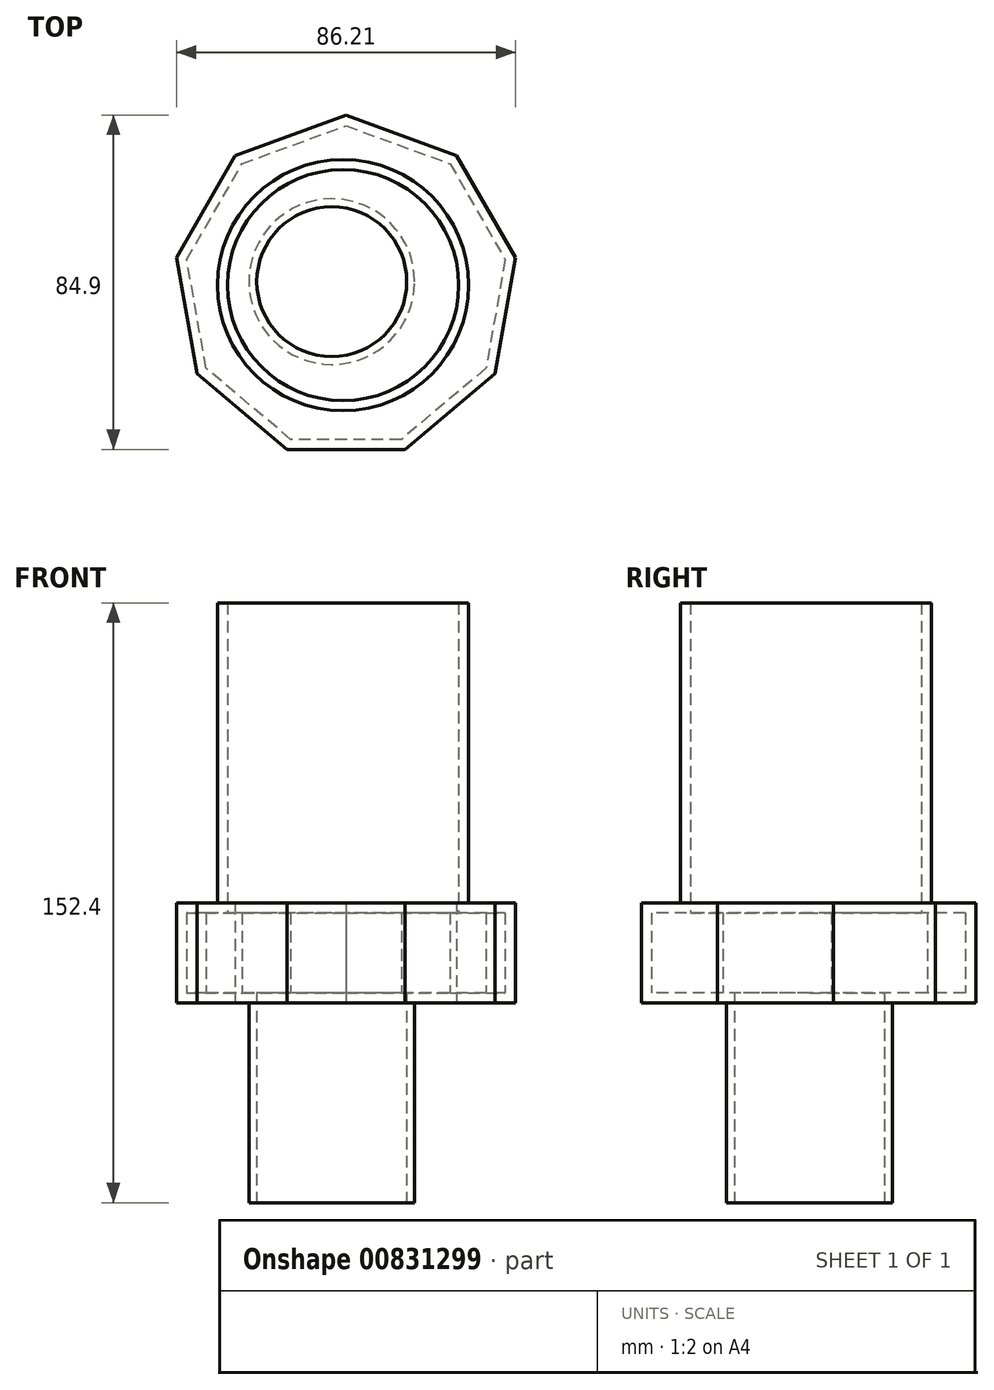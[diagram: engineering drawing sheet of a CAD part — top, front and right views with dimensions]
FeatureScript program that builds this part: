
annotation { "Feature Type Name" : "Feature", "Feature Type Description" : "" }
export const myFeature = defineFeature(function(context is Context, id is Id, definition is map)
    precondition{}
    {
        {
            var Q0;
            Q0=qCreatedBy(makeId("Top.planeOp"),FACE);
            var sketch = newSketch(context, id + "F0", { "sketchPlane" : qUnion([Q0])});
            skCircle(sketch, "E0", {"center": v(-10.72, 10.72) * mm, "radius": 31.9 * mm});
            skSolve(sketch);
        }
        {
            var Q0;
            Q0 = qSketchRegion(id + "F0", true);
            extrude(context, id + "F1", {"entities" : qUnion([Q0]), "depth" : 101.6 * mm, "offsetDistance" : 25.4 * mm});
        }
        {
            var Q0;
            Q0=qCreatedBy(makeId("Top.planeOp"),FACE);
            var sketch = newSketch(context, id + "F2", { "sketchPlane" : qUnion([Q0])});
            skCircle(sketch, "E1.cCircle", {"center": v(-9.98, 10.13) * mm, "radius": 41.13 * mm, "construction": true});
            skLineSegment(sketch, "E1.0", {"start": v(5, -31) * mm, "end": v(-24.95, -31) * mm});
            skLineSegment(sketch, "E1.1", {"start": v(-24.95, -31) * mm, "end": v(-47.88, -11.76) * mm});
            skLineSegment(sketch, "E1.2", {"start": v(-47.88, -11.76) * mm, "end": v(-53.08, 17.73) * mm});
            skLineSegment(sketch, "E1.3", {"start": v(-53.08, 17.73) * mm, "end": v(-38.11, 43.66) * mm});
            skLineSegment(sketch, "E1.4", {"start": v(-38.11, 43.66) * mm, "end": v(-9.98, 53.9) * mm});
            skLineSegment(sketch, "E1.5", {"start": v(-9.98, 53.9) * mm, "end": v(18.16, 43.66) * mm});
            skLineSegment(sketch, "E1.6", {"start": v(18.16, 43.66) * mm, "end": v(33.13, 17.73) * mm});
            skLineSegment(sketch, "E1.7", {"start": v(33.13, 17.73) * mm, "end": v(27.93, -11.76) * mm});
            skLineSegment(sketch, "E1.8", {"start": v(27.93, -11.76) * mm, "end": v(5, -31) * mm});
            skPoint(sketch, "E1.0.midPoint", {"position": v(-9.98, -31) * mm});
            skSolve(sketch);
        }
        {
            var Q0;
            Q0 = qSketchRegion(id + "F2", true);
            extrude(context, id + "F3", {"entities" : qUnion([Q0]), "operationType" : NewBodyOperationType.ADD, "depth" : 25.4 * mm, "offsetDistance" : 25.4 * mm});
        }
        {
            var Q0;
            Q0=makeQuery(id+"F1.opExtrude","CAP_FACE",FACE,{"disambiguationData":[OSD([sQuery(id+"F0.wireOp",EDGE,"E0")])],"isStart":false});
            shell(context, id + "F4", {"entities" : qUnion([Q0]), "thickness" : 2.54 * mm});
        }
        {
            var Q0;
            Q0=makeQuery(id+"F3.boolean.opBoolean","MERGE",FACE,{"derivedFrom":[makeQuery(id+"F1.opExtrude","CAP_FACE",FACE,{"disambiguationData":[OSD([sQuery(id+"F0.wireOp",EDGE,"E0")])],"isStart":true}),makeQuery(id+"F3.opExtrude","CAP_FACE",FACE,{"disambiguationData":[OSD([sQuery(id+"F2.wireOp",EDGE,"E1.0"),sQuery(id+"F2.wireOp",EDGE,"E1.1"),sQuery(id+"F2.wireOp",EDGE,"E1.2"),sQuery(id+"F2.wireOp",EDGE,"E1.3"),sQuery(id+"F2.wireOp",EDGE,"E1.4"),sQuery(id+"F2.wireOp",EDGE,"E1.5"),sQuery(id+"F2.wireOp",EDGE,"E1.6"),sQuery(id+"F2.wireOp",EDGE,"E1.7"),sQuery(id+"F2.wireOp",EDGE,"E1.8")])],"isStart":true})]});
            var sketch = newSketch(context, id + "F5", { "sketchPlane" : qUnion([Q0])});
            skCircle(sketch, "E2", {"center": v(-13.6, -11.6) * mm, "radius": 21.06 * mm});
            skSolve(sketch);
        }
        {
            var Q0;
            Q0=makeQuery(id+"F5.imprint","IMPRINT",FACE,{"disambiguationData":[TD([[makeQuery(id+"F5.imprint","IMPRINT",EDGE,{"derivedFrom":sQuery(id+"F5.wireOp",EDGE,"E2")}),1.0]])]});
            extrude(context, id + "F6", {"entities" : qUnion([Q0]), "operationType" : NewBodyOperationType.ADD, "depth" : 50.8 * mm, "offsetDistance" : 25.4 * mm});
        }
        {
            var Q0;
            Q0=makeQuery(id+"F6.opExtrude","CAP_FACE",FACE,{"disambiguationData":[OSD([sQuery(id+"F5.wireOp",EDGE,"E2")])],"isStart":false});
            var sketch = newSketch(context, id + "F7", { "sketchPlane" : qUnion([Q0])});
            skCircle(sketch, "E3", {"center": v(-13.6, -11.6) * mm, "radius": 17.24 * mm});
            skSolve(sketch);
        }
        {
            var Q0;
            Q0=sQuery(id+"F7.wireOp",VERTEX,"E3.center");
            var Q1;
            Q1=makeQuery(id+"F1.opExtrude","SWEPT_BODY",BODY,{"disambiguationData":[OSD([sQuery(id+"F0.wireOp",EDGE,"E0")])]});
            hole(context, id + "F8", {"style" : HoleStyle.SIMPLE, "endStyle" : HoleEndStyle.THROUGH, "holeDiameter" : 38.1 * mm, "majorDiameter" : 6.35 * mm, "isTappedThrough" : true, "tappedDepth" : 12.7 * mm, "tapClearance" : 3, "startFromSketch" : true, "locations" : qUnion([Q0]), "scope" : qUnion([Q1])});
        }
    });
